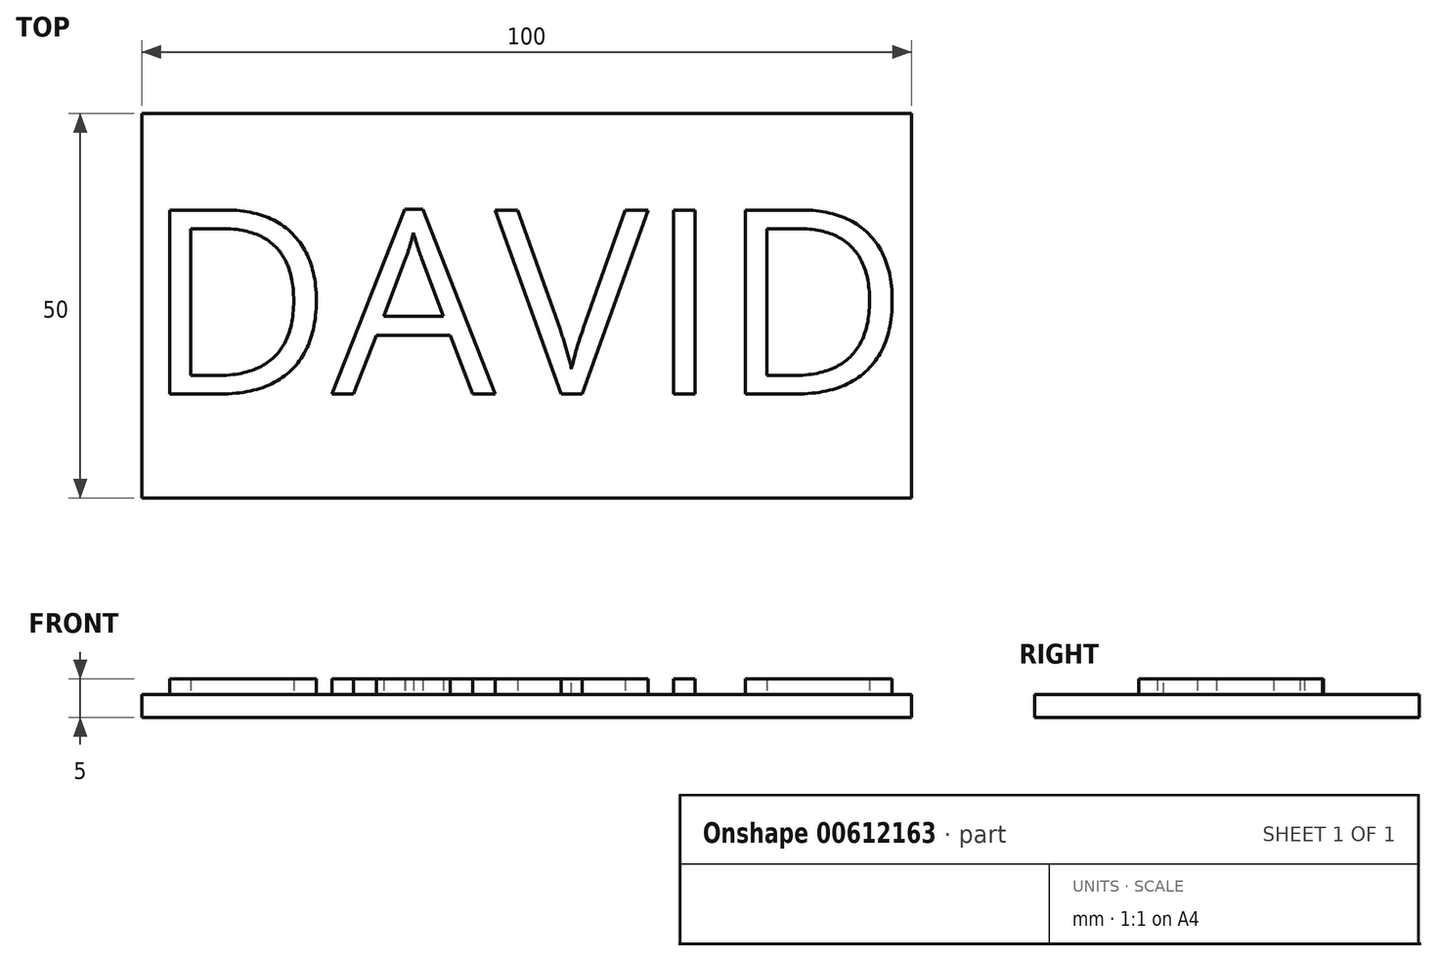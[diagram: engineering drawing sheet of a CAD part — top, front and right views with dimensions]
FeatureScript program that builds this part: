
annotation { "Feature Type Name" : "Feature", "Feature Type Description" : "" }
export const myFeature = defineFeature(function(context is Context, id is Id, definition is map)
    precondition{}
    {
        {
            var Q0;
            Q0=qCreatedBy(makeId("Top.planeOp"),FACE);
            var sketch = newSketch(context, id + "F0", { "sketchPlane" : qUnion([Q0])});
            skLineSegment(sketch, "E0.bottom", {"start": v(-50, 25) * mm, "end": v(50, 25) * mm});
            skLineSegment(sketch, "E0.top", {"start": v(-50, -25) * mm, "end": v(50, -25) * mm});
            skLineSegment(sketch, "E0.left", {"start": v(-50, 25) * mm, "end": v(-50, -25) * mm});
            skLineSegment(sketch, "E0.right", {"start": v(50, 25) * mm, "end": v(50, -25) * mm});
            skPoint(sketch, "E0.middle", {"position": v(0, 0) * mm});
            skSolve(sketch);
        }
        {
            var Q0;
            Q0=makeQuery(id+"F0.imprint","IMPRINT",FACE,{"disambiguationData":[TD([[makeQuery(id+"F0.imprint","IMPRINT",EDGE,{"derivedFrom":sQuery(id+"F0.wireOp",EDGE,"E0.bottom")}),-1.0]])]});
            extrude(context, id + "F1", {"entities" : qUnion([Q0]), "depth" : 3 * mm, "offsetDistance" : 25 * mm});
        }
        {
            var Q0;
            Q0=makeQuery(id+"F1.opExtrude","CAP_FACE",FACE,{"disambiguationData":[OSD([sQuery(id+"F0.wireOp",EDGE,"E0.bottom"),sQuery(id+"F0.wireOp",EDGE,"E0.top"),sQuery(id+"F0.wireOp",EDGE,"E0.left"),sQuery(id+"F0.wireOp",EDGE,"E0.right")])],"isStart":false});
            var sketch = newSketch(context, id + "F2", { "sketchPlane" : qUnion([Q0])});
            skText(sketch, "E1", { "text": "DAVID", "fontName": "OpenSans-Regular.ttf"});
            const initialGuessF2  = {"E1": [-0.0497, -0.01146, 1, 0, 0.0241]};
            skSetInitialGuess(sketch, initialGuessF2);
            skSolve(sketch);
        }
        {
            var Q0;
            Q0 = qSketchRegion(id + "F2", true);
            extrude(context, id + "F3", {"entities" : qUnion([Q0]), "operationType" : NewBodyOperationType.ADD, "depth" : 2 * mm, "offsetDistance" : 25 * mm});
        }
    });
